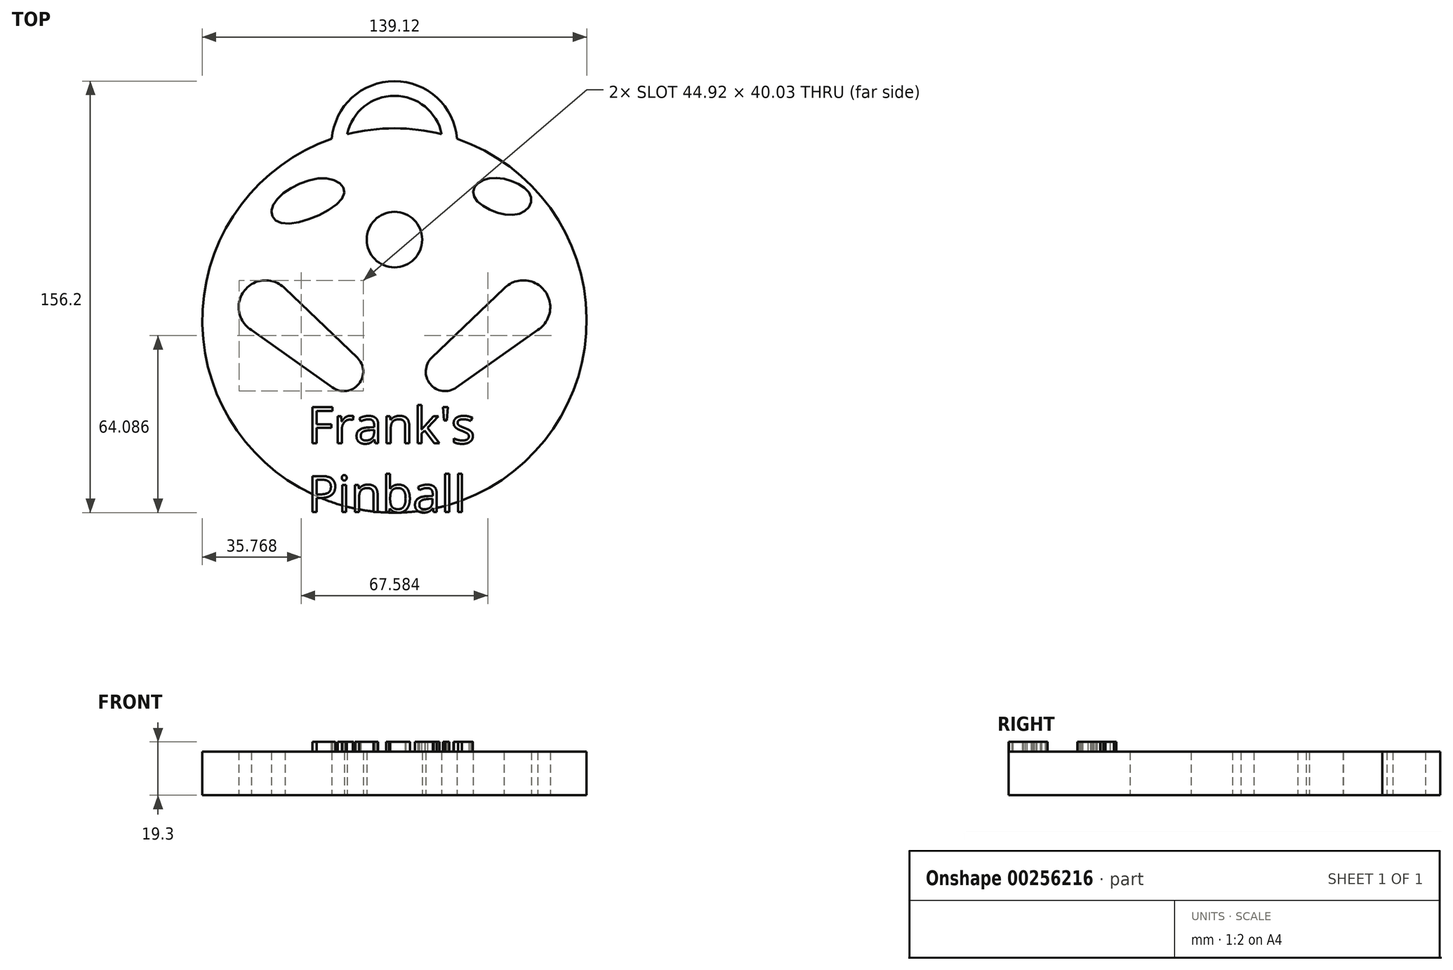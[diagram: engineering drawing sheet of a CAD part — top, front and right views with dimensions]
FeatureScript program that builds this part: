
annotation { "Feature Type Name" : "Feature", "Feature Type Description" : "" }
export const myFeature = defineFeature(function(context is Context, id is Id, definition is map)
    precondition{}
    {
        {
            var Q0;
            Q0=qCreatedBy(makeId("Top.planeOp"),FACE);
            var sketch = newSketch(context, id + "F0", { "sketchPlane" : qUnion([Q0])});
            skArc(sketch, "E0", {"start": v(17.1, 67.42) * mm, "mid": v(0, 69.56) * mm, "end": v(-17.1, 67.42) * mm});
            skCircle(sketch, "E1", {"center": v(0, 29.3) * mm, "radius": 10.05 * mm});
            skArc(sketch, "E2", {"start": v(13.5, -13.42) * mm, "mid": v(12.93, -23) * mm, "end": v(22.43, -24.26) * mm});
            skArc(sketch, "E3", {"start": v(51.85, -3.42) * mm, "mid": v(54.18, 10.98) * mm, "end": v(39.6, 11.55) * mm});
            skLineSegment(sketch, "E4", {"start": v(40.22, 12.14) * mm, "end": v(13.5, -13.42) * mm});
            skLineSegment(sketch, "E5", {"start": v(52.67, -2.84) * mm, "end": v(22.43, -24.26) * mm});
            skLineSegment(sketch, "E6.MirrorCS", {"start": v(-40.22, 12.14) * mm, "end": v(-13.5, -13.42) * mm});
            skLineSegment(sketch, "E7.MirrorCS", {"start": v(-52.67, -2.84) * mm, "end": v(-22.43, -24.26) * mm});
            skArc(sketch, "E8.MirrorCS", {"start": v(-13.5, -13.42) * mm, "mid": v(-12.93, -23) * mm, "end": v(-22.43, -24.26) * mm});
            skArc(sketch, "E9.MirrorCS", {"start": v(-51.85, -3.42) * mm, "mid": v(-54.18, 10.98) * mm, "end": v(-39.6, 11.55) * mm});
            skArc(sketch, "E10", {"start": v(22.68, 65.76) * mm, "mid": v(0, 86.64) * mm, "end": v(-22.68, 65.76) * mm});
            skArc(sketch, "E11", {"start": v(17.1, 67.42) * mm, "mid": v(0, 81.35) * mm, "end": v(-17.1, 67.42) * mm});
            skArc(sketch, "E12.trimOffspring", {"start": v(-22.68, 65.76) * mm, "mid": v(0, -69.56) * mm, "end": v(22.68, 65.76) * mm});
            skFitSpline(sketch, "E13", {"points": [v(-24.6, 51.47) * mm, v(-43.91, 41.82) * mm, v(-40.8, 35.28) * mm, v(-18.37, 45.24) * mm, v(-24.6, 51.47) * mm]});
            skFitSpline(sketch, "E14", {"points": [v(34.27, 51.47) * mm, v(49.22, 45.24) * mm, v(44.22, 38.37) * mm, v(28.65, 45.24) * mm, v(34.27, 51.47) * mm]});
            skSolve(sketch);
        }
        {
            var Q0;
            Q0=makeQuery(id+"F0.imprint","IMPRINT",FACE,{"disambiguationData":[TD([[makeQuery(id+"F0.imprint","IMPRINT",EDGE,{"derivedFrom":sQuery(id+"F0.wireOp",EDGE,"E0")}),1.0]])]});
            extrude(context, id + "F1", {"entities" : qUnion([Q0]), "depth" : 15.75 * mm});
        }
        {
            var Q0;
            Q0=makeQuery(id+"F1.opExtrude","CAP_FACE",FACE,{"disambiguationData":[OSD([sQuery(id+"F0.wireOp",EDGE,"E0"),sQuery(id+"F0.wireOp",EDGE,"E1"),sQuery(id+"F0.wireOp",EDGE,"E2"),sQuery(id+"F0.wireOp",EDGE,"E3"),sQuery(id+"F0.wireOp",EDGE,"E4"),sQuery(id+"F0.wireOp",EDGE,"E5"),sQuery(id+"F0.wireOp",EDGE,"E6.MirrorCS"),sQuery(id+"F0.wireOp",EDGE,"E7.MirrorCS"),sQuery(id+"F0.wireOp",EDGE,"E8.MirrorCS"),sQuery(id+"F0.wireOp",EDGE,"E9.MirrorCS"),sQuery(id+"F0.wireOp",EDGE,"E10"),sQuery(id+"F0.wireOp",EDGE,"E11"),sQuery(id+"F0.wireOp",EDGE,"E12.trimOffspring"),sQuery(id+"F0.wireOp",EDGE,"E13"),sQuery(id+"F0.wireOp",EDGE,"E14")])],"isStart":false});
            var sketch = newSketch(context, id + "F2", { "sketchPlane" : qUnion([Q0])});
            skText(sketch, "E15", { "text": "Frank\'s \nPinball", "fontName": "OpenSans-Regular.ttf"});
            const initialGuessF2  = {"E15": [-0.03152, -0.04448, 1, 0, 0.01318]};
            skSetInitialGuess(sketch, initialGuessF2);
            skSolve(sketch);
        }
        {
            var Q0;
            Q0 = qSketchRegion(id + "F2", true);
            extrude(context, id + "F3", {"entities" : qUnion([Q0]), "operationType" : NewBodyOperationType.ADD, "depth" : 3.56 * mm});
        }
    });
